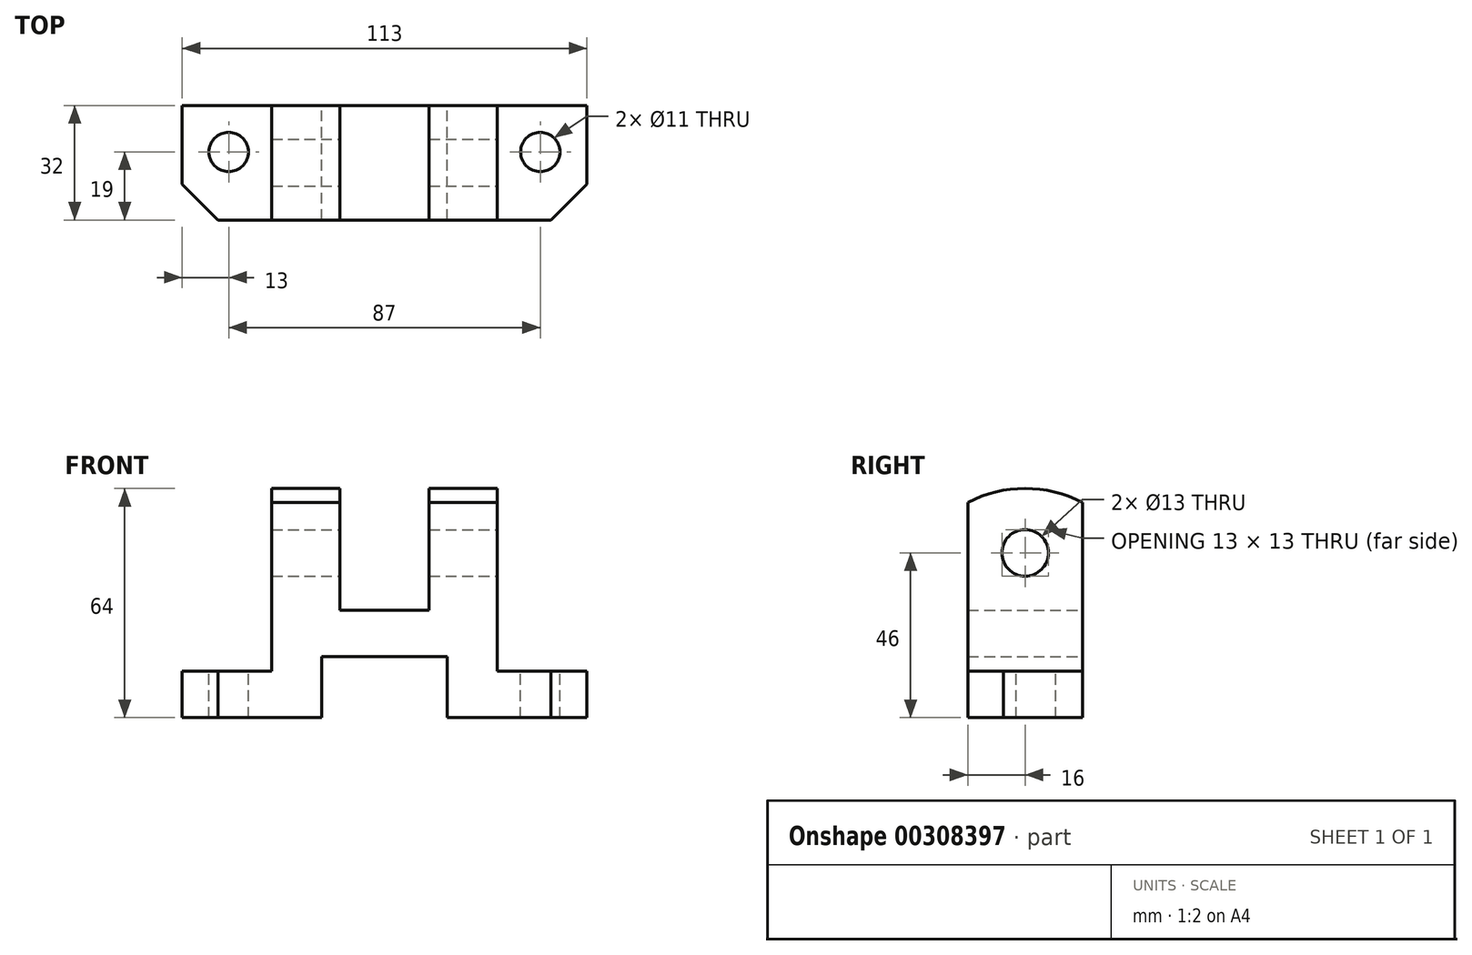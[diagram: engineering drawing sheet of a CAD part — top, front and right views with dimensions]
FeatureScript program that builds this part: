
annotation { "Feature Type Name" : "Feature", "Feature Type Description" : "" }
export const myFeature = defineFeature(function(context is Context, id is Id, definition is map)
    precondition{}
    {
        {
            var Q0;
            Q0=qCreatedBy(makeId("Front.planeOp"),FACE);
            var sketch = newSketch(context, id + "F0", { "sketchPlane" : qUnion([Q0])});
            skLineSegment(sketch, "E0", {"start": v(0, 0) * mm, "end": v(0, 13) * mm});
            skLineSegment(sketch, "E1", {"start": v(0, 13) * mm, "end": v(25, 13) * mm});
            skLineSegment(sketch, "E2", {"start": v(25, 13) * mm, "end": v(25, 64) * mm});
            skLineSegment(sketch, "E3", {"start": v(25, 64) * mm, "end": v(44, 64) * mm});
            skLineSegment(sketch, "E4", {"start": v(44, 64) * mm, "end": v(44, 30) * mm});
            skLineSegment(sketch, "E5", {"start": v(44, 30) * mm, "end": v(69, 30) * mm});
            skLineSegment(sketch, "E6", {"start": v(69, 30) * mm, "end": v(69, 64) * mm});
            skLineSegment(sketch, "E7", {"start": v(69, 64) * mm, "end": v(88, 64) * mm});
            skLineSegment(sketch, "E8", {"start": v(88, 64) * mm, "end": v(88, 13) * mm});
            skLineSegment(sketch, "E9", {"start": v(88, 13) * mm, "end": v(113, 13) * mm});
            skLineSegment(sketch, "E10", {"start": v(113, 13) * mm, "end": v(113, 0) * mm});
            skLineSegment(sketch, "E11", {"start": v(113, 0) * mm, "end": v(74, 0) * mm});
            skLineSegment(sketch, "E12", {"start": v(74, 0) * mm, "end": v(74, 17) * mm});
            skLineSegment(sketch, "E13", {"start": v(74, 17) * mm, "end": v(39, 17) * mm});
            skLineSegment(sketch, "E14", {"start": v(39, 17) * mm, "end": v(39, 0) * mm});
            skLineSegment(sketch, "E15", {"start": v(39, 0) * mm, "end": v(0, 0) * mm});
            skSolve(sketch);
        }
        {
            var Q0;
            Q0 = qSketchRegion(id + "F0", true);
            extrude(context, id + "F1", {"entities" : qUnion([Q0]), "depth" : 32 * mm});
        }
        {
            var Q0;
            Q0=makeQuery(id+"F1.opExtrude","SWEPT_FACE",FACE,{"disambiguationData":[OSD([sQuery(id+"F0.wireOp",EDGE,"E8")])]});
            var sketch = newSketch(context, id + "F2", { "sketchPlane" : qUnion([Q0])});
            skArc(sketch, "E16", {"start": v(0, 60.13) * mm, "mid": v(-16, 64) * mm, "end": v(-32, 60.13) * mm});
            skLineSegment(sketch, "E17", {"start": v(-32, 13) * mm, "end": v(-32, 60.13) * mm});
            skLineSegment(sketch, "E18", {"start": v(0, 13) * mm, "end": v(0, 60.13) * mm});
            skSolve(sketch);
        }
        {
            var Q0;
            Q0 = qSketchRegion(id + "F2", true);
            var Q1;
            {var subQ0=sQuery(id+"F2.wireOp",EDGE,"E16");var subQ1=sQuery(id+"F0.wireOp",EDGE,"E8");var subQ2=makeQuery(id+"F1.opExtrude","CAP_EDGE",EDGE,{"disambiguationData":[OSD([subQ1])],"isStart":false});var subQ3=makeQuery(id+"F2.imprint","INTERSECT",VERTEX,{"derivedFrom":[subQ2,subQ0,sQuery(id+"F2.wireOp",EDGE,"E17")]});Q1=makeQuery(id+"F2.imprint","IMPRINT",FACE,{"disambiguationData":[TD([[makeQuery(id+"F2.imprint","IMPRINT",EDGE,{"disambiguationData":[TD([[subQ3,1.0]])],"derivedFrom":subQ0}),-1.0]])]});}
            var Q2;
            {var subQ0=sQuery(id+"F2.wireOp",EDGE,"E16");var subQ1=sQuery(id+"F0.wireOp",EDGE,"E8");var subQ2=makeQuery(id+"F1.opExtrude","CAP_EDGE",EDGE,{"disambiguationData":[OSD([subQ1])],"isStart":true});var subQ3=makeQuery(id+"F2.imprint","INTERSECT",VERTEX,{"derivedFrom":[subQ2,subQ0,sQuery(id+"F2.wireOp",EDGE,"E18")]});Q2=makeQuery(id+"F2.imprint","IMPRINT",FACE,{"disambiguationData":[TD([[makeQuery(id+"F2.imprint","IMPRINT",EDGE,{"disambiguationData":[TD([[subQ3,-1.0]])],"derivedFrom":subQ0}),-1.0]])]});}
            extrude(context, id + "F3", {"entities" : qUnion([Q0, Q1, Q2]), "operationType" : NewBodyOperationType.REMOVE, "endBound" : BoundingType.THROUGH_ALL, "oppositeDirection" : true, "depth" : 25 * mm});
        }
        {
            var Q0;
            Q0=makeQuery(id+"F1.opExtrude","SWEPT_FACE",FACE,{"disambiguationData":[OSD([sQuery(id+"F0.wireOp",EDGE,"E8")])]});
            var sketch = newSketch(context, id + "F4", { "sketchPlane" : qUnion([Q0])});
            skCircle(sketch, "E19", {"center": v(-16, 46) * mm, "radius": 6.5 * mm});
            skPoint(sketch, "E19.centerSnap0", {"position": v(-16, 64) * mm});
            skSolve(sketch);
        }
        {
            var Q0;
            Q0 = qSketchRegion(id + "F4", true);
            extrude(context, id + "F5", {"entities" : qUnion([Q0]), "operationType" : NewBodyOperationType.REMOVE, "endBound" : BoundingType.THROUGH_ALL, "oppositeDirection" : true, "depth" : 25 * mm});
        }
        {
            var Q0;
            Q0=makeQuery(id+"F1.opExtrude","CAP_EDGE",EDGE,{"disambiguationData":[OSD([sQuery(id+"F0.wireOp",EDGE,"E10")])],"isStart":false});
            var Q1;
            Q1=makeQuery(id+"F1.opExtrude","CAP_EDGE",EDGE,{"disambiguationData":[OSD([sQuery(id+"F0.wireOp",EDGE,"E0")])],"isStart":false});
            chamfer(context, id + "F6", {"entities" : qUnion([Q0, Q1]), "width" : 10 * mm, "tangentPropagation" : true});
        }
        {
            var Q0;
            Q0=makeQuery(id+"F1.opExtrude","SWEPT_FACE",FACE,{"disambiguationData":[OSD([sQuery(id+"F0.wireOp",EDGE,"E9")])]});
            var sketch = newSketch(context, id + "F7", { "sketchPlane" : qUnion([Q0])});
            skCircle(sketch, "E20", {"center": v(100, -13) * mm, "radius": 5.5 * mm});
            skCircle(sketch, "E21", {"center": v(13, -13) * mm, "radius": 5.5 * mm});
            skSolve(sketch);
        }
        {
            var Q0;
            Q0 = qSketchRegion(id + "F7", true);
            extrude(context, id + "F8", {"entities" : qUnion([Q0]), "operationType" : NewBodyOperationType.REMOVE, "endBound" : BoundingType.THROUGH_ALL, "oppositeDirection" : true, "depth" : 25 * mm});
        }
    });
